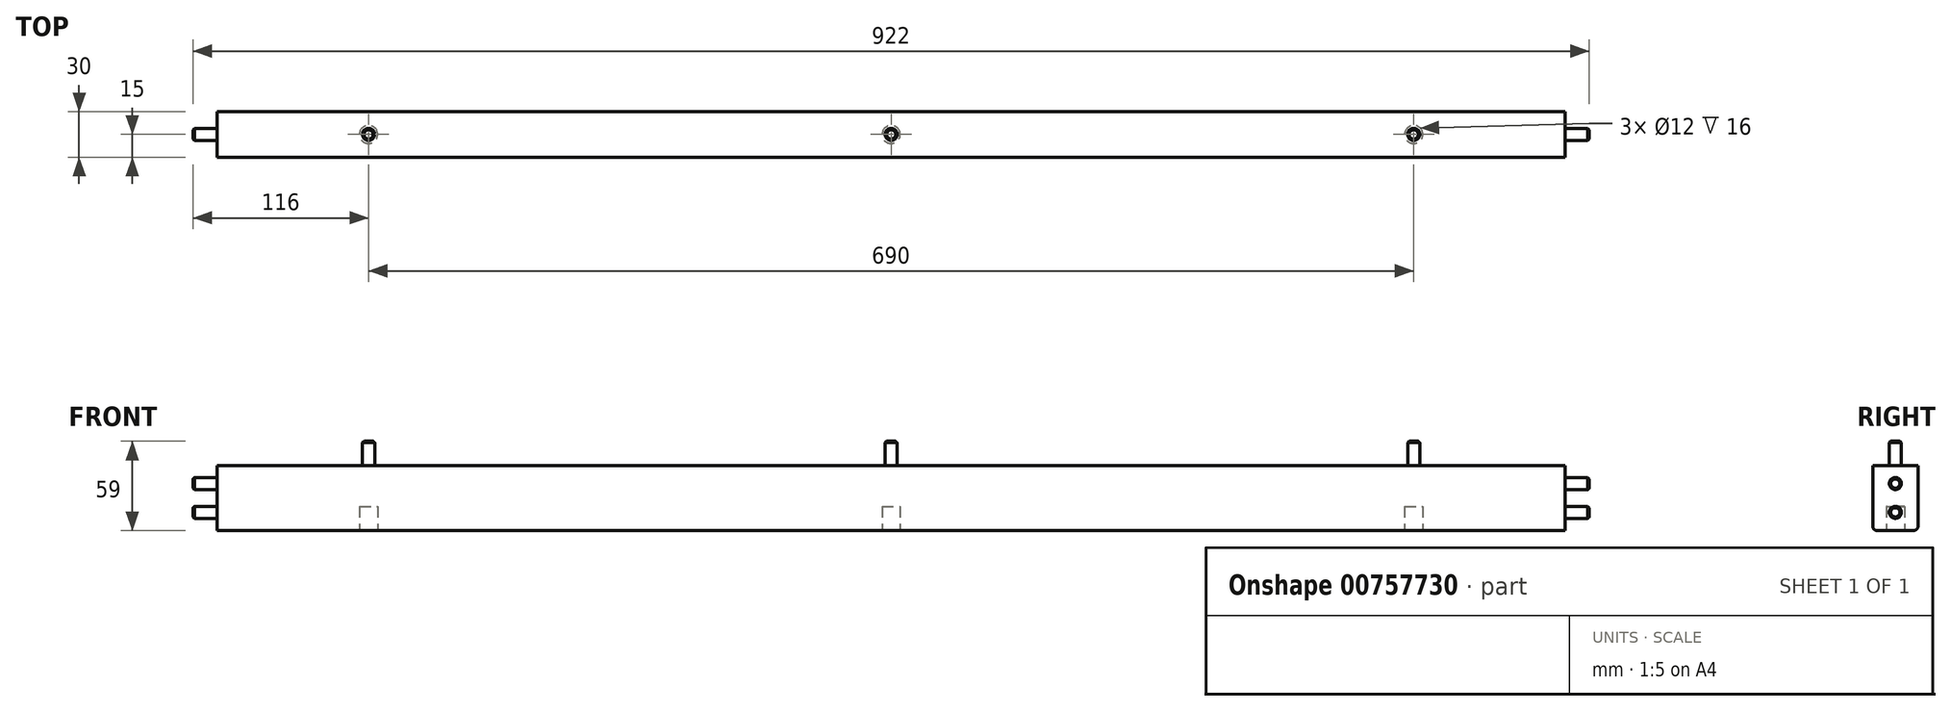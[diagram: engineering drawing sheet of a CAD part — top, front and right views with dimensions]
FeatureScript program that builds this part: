
annotation { "Feature Type Name" : "Feature", "Feature Type Description" : "" }
export const myFeature = defineFeature(function(context is Context, id is Id, definition is map)
    precondition{}
    {
        {
            var Q0;
            Q0=qCreatedBy(makeId("Front.planeOp"),FACE);
            var sketch = newSketch(context, id + "F0", { "sketchPlane" : qUnion([Q0])});
            skLineSegment(sketch, "E0.bottom", {"start": v(445, 21.5) * mm, "end": v(-445, 21.5) * mm});
            skLineSegment(sketch, "E0.top", {"start": v(445, -21.5) * mm, "end": v(-445, -21.5) * mm});
            skLineSegment(sketch, "E0.left", {"start": v(445, 21.5) * mm, "end": v(445, -21.5) * mm});
            skLineSegment(sketch, "E0.right", {"start": v(-445, 21.5) * mm, "end": v(-445, -21.5) * mm});
            skPoint(sketch, "E0.middle", {"position": v(0, 0) * mm});
            skSolve(sketch);
        }
        {
            var Q0;
            Q0 = qSketchRegion(id + "F0", true);
            extrude(context, id + "F1", {"entities" : qUnion([Q0]), "oppositeDirection" : true, "depth" : 30 * mm, "offsetDistance" : 25 * mm});
        }
        {
            var Q0;
            Q0=makeQuery(id+"F1.opExtrude","SWEPT_FACE",FACE,{"disambiguationData":[OSD([sQuery(id+"F0.wireOp",EDGE,"E0.left")])]});
            var sketch = newSketch(context, id + "F2", { "sketchPlane" : qUnion([Q0])});
            skLineSegment(sketch, "E1", {"start": v(15, 21.5) * mm, "end": v(15, -32.62) * mm, "construction": true});
            skCircle(sketch, "E2", {"center": v(15, 9.5) * mm, "radius": 4 * mm});
            skCircle(sketch, "E3", {"center": v(15, -9.5) * mm, "radius": 4 * mm});
            skSolve(sketch);
        }
        {
            var Q0;
            Q0=makeQuery(id+"F2.imprint","IMPRINT",FACE,{"disambiguationData":[TD([[makeQuery(id+"F2.imprint","IMPRINT",EDGE,{"derivedFrom":sQuery(id+"F2.wireOp",EDGE,"E2")}),1.0]])]});
            var Q1;
            Q1=makeQuery(id+"F2.imprint","IMPRINT",FACE,{"disambiguationData":[TD([[makeQuery(id+"F2.imprint","IMPRINT",EDGE,{"derivedFrom":sQuery(id+"F2.wireOp",EDGE,"E3")}),1.0]])]});
            extrude(context, id + "F3", {"entities" : qUnion([Q0, Q1]), "operationType" : NewBodyOperationType.ADD, "depth" : 16 * mm, "offsetDistance" : 25 * mm});
        }
        {
            var Q0;
            Q0=makeQuery(id+"F3.opExtrude","CAP_EDGE",EDGE,{"disambiguationData":[OSD([sQuery(id+"F2.wireOp",EDGE,"E2")])],"isStart":false});
            var Q1;
            Q1=makeQuery(id+"F3.opExtrude","CAP_EDGE",EDGE,{"disambiguationData":[OSD([sQuery(id+"F2.wireOp",EDGE,"E3")])],"isStart":false});
            chamfer(context, id + "F4", {"entities" : qUnion([Q0, Q1]), "width" : 1 * mm, "tangentPropagation" : true});
        }
        {
            var Q0;
            Q0=makeQuery(id+"F1.opExtrude","SWEPT_FACE",FACE,{"disambiguationData":[OSD([sQuery(id+"F0.wireOp",EDGE,"E0.right")])]});
            var sketch = newSketch(context, id + "F5", { "sketchPlane" : qUnion([Q0])});
            skLineSegment(sketch, "E4", {"start": v(-15, 21.5) * mm, "end": v(-15, -21.5) * mm, "construction": true});
            skCircle(sketch, "E5", {"center": v(-15, 9.5) * mm, "radius": 4 * mm});
            skCircle(sketch, "E6", {"center": v(-15, -9.5) * mm, "radius": 4 * mm});
            skSolve(sketch);
        }
        {
            var Q0;
            Q0=makeQuery(id+"F5.imprint","IMPRINT",FACE,{"disambiguationData":[TD([[makeQuery(id+"F5.imprint","IMPRINT",EDGE,{"derivedFrom":sQuery(id+"F5.wireOp",EDGE,"E5")}),1.0]])]});
            var Q1;
            Q1=makeQuery(id+"F5.imprint","IMPRINT",FACE,{"disambiguationData":[TD([[makeQuery(id+"F5.imprint","IMPRINT",EDGE,{"derivedFrom":sQuery(id+"F5.wireOp",EDGE,"E6")}),1.0]])]});
            extrude(context, id + "F6", {"entities" : qUnion([Q0, Q1]), "operationType" : NewBodyOperationType.ADD, "depth" : 16 * mm, "offsetDistance" : 25 * mm});
        }
        {
            var Q0;
            Q0=makeQuery(id+"F6.opExtrude","CAP_EDGE",EDGE,{"disambiguationData":[OSD([sQuery(id+"F5.wireOp",EDGE,"E5")])],"isStart":false});
            var Q1;
            Q1=makeQuery(id+"F6.opExtrude","CAP_EDGE",EDGE,{"disambiguationData":[OSD([sQuery(id+"F5.wireOp",EDGE,"E6")])],"isStart":false});
            chamfer(context, id + "F7", {"entities" : qUnion([Q0, Q1]), "width" : 1 * mm, "tangentPropagation" : true});
        }
        {
            var Q0;
            Q0=makeQuery(id+"F1.opExtrude","CAP_EDGE",EDGE,{"disambiguationData":[OSD([sQuery(id+"F0.wireOp",EDGE,"E0.top")])],"isStart":false});
            var Q1;
            Q1=makeQuery(id+"F1.opExtrude","CAP_EDGE",EDGE,{"disambiguationData":[OSD([sQuery(id+"F0.wireOp",EDGE,"E0.top")])],"isStart":true});
            fillet(context, id + "F8", {"entities" : qUnion([Q0, Q1]), "radius" : 3 * mm, "tangentPropagation" : true, "allowEdgeOverflow" : false});
        }
        {
            var Q0;
            Q0=makeQuery(id+"F1.opExtrude","SWEPT_FACE",FACE,{"disambiguationData":[OSD([sQuery(id+"F0.wireOp",EDGE,"E0.top")])]});
            var sketch = newSketch(context, id + "F9", { "sketchPlane" : qUnion([Q0])});
            skLineSegment(sketch, "E7", {"start": v(-445, -15) * mm, "end": v(445, -15) * mm, "construction": true});
            skCircle(sketch, "E8", {"center": v(-345, -15) * mm, "radius": 6 * mm});
            skCircle(sketch, "E9", {"center": v(0, -15) * mm, "radius": 6 * mm});
            skCircle(sketch, "E10", {"center": v(345, -15) * mm, "radius": 6 * mm});
            skSolve(sketch);
        }
        {
            var Q0;
            Q0=makeQuery(id+"F9.imprint","IMPRINT",FACE,{"disambiguationData":[TD([[makeQuery(id+"F9.imprint","IMPRINT",EDGE,{"derivedFrom":sQuery(id+"F9.wireOp",EDGE,"E8")}),1.0]])]});
            var Q1;
            Q1=makeQuery(id+"F9.imprint","IMPRINT",FACE,{"disambiguationData":[TD([[makeQuery(id+"F9.imprint","IMPRINT",EDGE,{"derivedFrom":sQuery(id+"F9.wireOp",EDGE,"E9")}),1.0]])]});
            var Q2;
            Q2=makeQuery(id+"F9.imprint","IMPRINT",FACE,{"disambiguationData":[TD([[makeQuery(id+"F9.imprint","IMPRINT",EDGE,{"derivedFrom":sQuery(id+"F9.wireOp",EDGE,"E10")}),1.0]])]});
            extrude(context, id + "F10", {"entities" : qUnion([Q0, Q1, Q2]), "operationType" : NewBodyOperationType.REMOVE, "oppositeDirection" : true, "depth" : 16 * mm, "offsetDistance" : 25 * mm});
        }
        {
            var Q0;
            Q0=makeQuery(id+"F1.opExtrude","SWEPT_FACE",FACE,{"disambiguationData":[OSD([sQuery(id+"F0.wireOp",EDGE,"E0.bottom")])]});
            var sketch = newSketch(context, id + "F11", { "sketchPlane" : qUnion([Q0])});
            skLineSegment(sketch, "E11", {"start": v(-445, 15) * mm, "end": v(445, 15) * mm, "construction": true});
            skCircle(sketch, "E12", {"center": v(0, 15) * mm, "radius": 4 * mm});
            skCircle(sketch, "E13", {"center": v(-345, 15) * mm, "radius": 4 * mm});
            skCircle(sketch, "E14", {"center": v(345, 15) * mm, "radius": 4 * mm});
            skSolve(sketch);
        }
        {
            var Q0;
            Q0 = qSketchRegion(id + "F11", true);
            extrude(context, id + "F12", {"entities" : qUnion([Q0]), "operationType" : NewBodyOperationType.ADD, "depth" : 16 * mm, "offsetDistance" : 25 * mm});
        }
        {
            var Q0;
            Q0=makeQuery(id+"F12.opExtrude","CAP_EDGE",EDGE,{"disambiguationData":[OSD([sQuery(id+"F11.wireOp",EDGE,"E13")])],"isStart":false});
            var Q1;
            Q1=makeQuery(id+"F12.opExtrude","CAP_EDGE",EDGE,{"disambiguationData":[OSD([sQuery(id+"F11.wireOp",EDGE,"E12")])],"isStart":false});
            var Q2;
            Q2=makeQuery(id+"F12.opExtrude","CAP_EDGE",EDGE,{"disambiguationData":[OSD([sQuery(id+"F11.wireOp",EDGE,"E14")])],"isStart":false});
            chamfer(context, id + "F13", {"entities" : qUnion([Q0, Q1, Q2]), "width" : 1 * mm, "tangentPropagation" : true});
        }
    });
